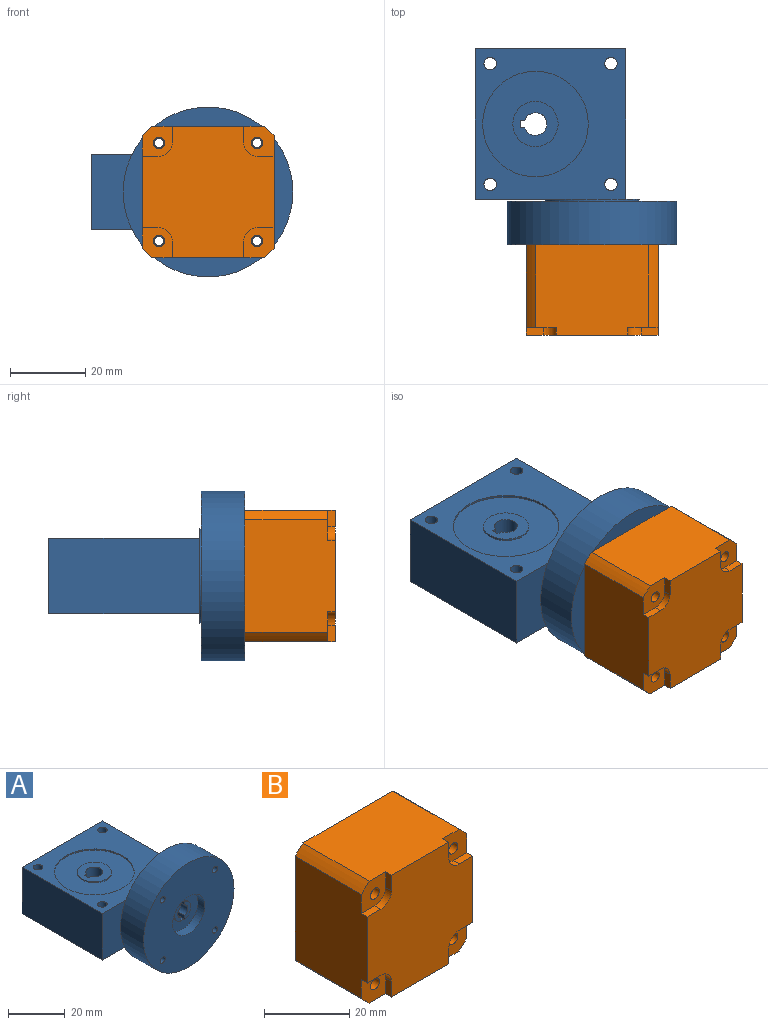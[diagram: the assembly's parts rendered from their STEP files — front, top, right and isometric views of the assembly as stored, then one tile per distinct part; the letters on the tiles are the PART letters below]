
ASSEMBLY  parts=2 mates=1
PART A: 51 faces, bbox 53.5x52x45 mm
  f0: plane 12x12mm, normal (0,0,1), area 82.7mm2, adj f44,f45,f46,f47,f48
  f1: plane 40x40mm, normal (0,0,1), area 950mm2, adj f6,f7,f8,f9,f10,f12,f13,f14
  f2: plane 12x12mm, normal (0,0,-1), area 82.7mm2, adj f43,f44,f45,f46,f47
  f3: cylinder r=4mm len=7.75mm, axis (0,1,0), area 4.2mm2, adj f5,f29,f34,f39
  f4: plane 7.75x3mm, normal (0,-1,0), area 12.3mm2, adj f30,f31,f33,f37
  f5: plane 7.75x3mm, normal (0,-1,0), area 12.3mm2, adj f3,f31,f34,f39
  f6: plane 1.5x1.33mm, normal (0,-1,0), area 0.9mm2, adj f1,f8,f19
  f7: plane 23.5x20mm, normal (0,-1,0), area 400.1mm2, adj f1,f10,f16,f19
  f8: plane 40x20mm, normal (1,0,0), area 800mm2, adj f1,f6,f9,f11,f16,f20
  f9: plane 40x20mm, normal (0,1,0), area 800mm2, adj f1,f8,f10,f16
  f10: plane 40x20mm, normal (-1,0,0), area 800mm2, adj f1,f7,f9,f16
  f11: plane 1.5x1.33mm, normal (0,-1,0), area 0.9mm2, adj f8,f16,f19
  f12: cylinder r=1.65mm len=20mm, axis (0,0,-1), area 207.3mm2, adj f1,f16
  f13: cylinder r=1.65mm len=20mm, axis (0,0,-1), area 207.3mm2, adj f1,f16
  f14: cylinder r=1.65mm len=20mm, axis (0,0,-1), area 207.3mm2, adj f1,f16
  f15: cylinder r=1.65mm len=20mm, axis (0,0,-1), area 207.3mm2, adj f1,f16
  f16: plane 40x40mm, normal (0,0,-1), area 950mm2, adj f7,f8,f9,f10,f11,f12,f13,f14
  f17: plane 15x2.5mm, normal (0,1,0), area 25.5mm2, adj f16,f19
  f18: plane 15x2.5mm, normal (0,1,0), area 25.5mm2, adj f1,f19
  f19: cylinder r=12.5mm len=25mm, axis (0,1,0), area 39.3mm2, adj f6,f7,f11,f17,f18,f20,f23
  f20: plane 17.35x3.5mm, normal (0,1,0), area 41.8mm2, adj f8,f19
  f21: cylinder r=22.5mm len=45mm, axis (0,1,0), area 1625.8mm2, adj f22,f23
  f22: plane 45x45mm, normal (0,-1,0), area 1369.7mm2, adj f21,f24,f25,f26,f27,f28
  f23: plane 45x45mm, normal (0,1,0), area 1079.9mm2, adj f19,f21,f24,f25,f26,f27
  f24: cylinder r=1.25mm len=11.5mm, axis (0,-1,0), area 90.3mm2, adj f22,f23
  f25: cylinder r=1.25mm len=11.5mm, axis (0,-1,0), area 90.3mm2, adj f22,f23
  f26: cylinder r=1.25mm len=11.5mm, axis (0,-1,0), area 90.3mm2, adj f22,f23
  f27: cylinder r=1.25mm len=11.5mm, axis (0,-1,0), area 90.3mm2, adj f22,f23
  f28: cylinder r=8mm len=16mm, axis (0,-1,0), area 170.9mm2, adj f22,f29
  f29: plane 16x16mm, normal (0,-1,0), area 150.8mm2, adj f3,f28,f30,f35,f38
  f30: cylinder r=4mm len=7.75mm, axis (0,1,0), area 4.2mm2, adj f4,f29,f33,f37
  f31: cylinder r=2.5mm len=15mm, axis (0,-1,0), area 215mm2, adj f4,f5,f32,f33,f34,f36,f37,f39
  f32: plane 5x5mm, normal (0,-1,0), area 19.6mm2, adj f31
  f33: plane 5x1.58mm, normal (-1,0,0), area 7.9mm2, adj f4,f30,f31,f35,f36
  f34: plane 5x1.58mm, normal (1,0,0), area 7.9mm2, adj f3,f5,f31,f35,f36
  f35: cylinder r=4mm len=4.6mm, axis (0,-1,0), area 9.3mm2, adj f29,f33,f34,f36
  f36: plane 2x1.71mm, normal (0,-1,0), area 3.1mm2, adj f31,f33,f34,f35
  f37: plane 5x1.58mm, normal (-1,0,0), area 7.9mm2, adj f4,f30,f31,f38,f40
  f38: cylinder r=4mm len=4.6mm, axis (0,-1,0), area 9.3mm2, adj f29,f37,f39,f40
  f39: plane 5x1.58mm, normal (1,0,0), area 7.9mm2, adj f3,f5,f31,f38,f40
  f40: plane 2x1.71mm, normal (0,-1,0), area 3.1mm2, adj f31,f37,f38,f39
  f41: cylinder r=14mm len=28mm, axis (0,0,-1), area 44mm2, adj f16,f42
  f42: plane 28x28mm, normal (0,0,-1), area 502.7mm2, adj f41,f43
  f43: cylinder r=6mm len=12mm, axis (0,0,1), area 18.8mm2, adj f2,f42
  f44: plane 20x1.17mm, normal (0,1,0), area 23.4mm2, adj f0,f2,f45,f47
  f45: plane 20x2mm, normal (1,0,0), area 40mm2, adj f0,f2,f44,f46
  f46: plane 20x1.17mm, normal (0,-1,0), area 23.4mm2, adj f0,f2,f45,f47
  f47: cylinder r=3mm len=20mm, axis (0,0,-1), area 336.2mm2, adj f0,f2,f44,f46
  f48: cylinder r=6mm len=12mm, axis (0,0,1), area 18.8mm2, adj f0,f50
  f49: cylinder r=14mm len=28mm, axis (0,0,1), area 44mm2, adj f1,f50
  f50: plane 28x28mm, normal (0,0,1), area 502.7mm2, adj f48,f49
PART B: 35 faces, bbox 35x39x35 mm
  f0: cylinder r=23mm len=22mm, axis (0,1,0), area 80.2mm2, adj f1,f11,f13,f24
  f1: plane 29.85x24mm, normal (0,0,-1), area 694.7mm2, adj f0,f2,f12,f13,f22,f24,f26,f27
  f2: cylinder r=23mm len=22mm, axis (0,1,0), area 80.2mm2, adj f1,f3,f13,f27
  f3: plane 29.85x24mm, normal (1,0,0), area 694.7mm2, adj f2,f4,f12,f13,f15,f17,f27,f28
  f4: cylinder r=23mm len=22mm, axis (0,1,0), area 80.2mm2, adj f3,f5,f13,f17
  f5: plane 29.85x24mm, normal (0,0,1), area 694.7mm2, adj f4,f6,f12,f13,f16,f17,f20,f21
  f6: cylinder r=23mm len=22mm, axis (0,1,0), area 80.2mm2, adj f5,f11,f13,f21
  f7: cylinder r=1.5mm len=22mm, axis (0,1,0), area 207.3mm2, adj f13,f17
  f8: cylinder r=1.5mm len=22mm, axis (0,1,0), area 207.3mm2, adj f13,f21
  f9: cylinder r=1.5mm len=22mm, axis (0,1,0), area 207.3mm2, adj f13,f24
  f10: cylinder r=1.5mm len=22mm, axis (0,1,0), area 207.3mm2, adj f13,f27
  f11: plane 29.85x24mm, normal (-1,0,0), area 694.7mm2, adj f0,f6,f12,f13,f18,f21,f23,f24
  f12: plane 35x35mm, normal (0,-1,0), area 979.5mm2, adj f1,f3,f5,f11,f14,f15,f16,f18
  f13: plane 35x35mm, normal (0,1,0), area 1105.6mm2, adj f0,f1,f2,f3,f4,f5,f6,f7
  f14: cylinder r=3.5mm len=3.5mm, axis (0,-1,0), area 11mm2, adj f12,f15,f16,f17
  f15: plane 4.5x2mm, normal (0,0,1), area 9mm2, adj f3,f12,f14,f17
  f16: plane 4.5x2mm, normal (1,0,0), area 9mm2, adj f5,f12,f14,f17
  f17: plane 8x8mm, normal (0,-1,0), area 51.2mm2, adj f3,f4,f5,f7,f14,f15,f16
  f18: plane 4.5x2mm, normal (0,0,1), area 9mm2, adj f11,f12,f19,f21
  f19: cylinder r=3.5mm len=3.5mm, axis (0,-1,0), area 11mm2, adj f12,f18,f20,f21
  f20: plane 4.5x2mm, normal (-1,0,0), area 9mm2, adj f5,f12,f19,f21
  f21: plane 8x8mm, normal (0,-1,0), area 51.2mm2, adj f5,f6,f8,f11,f18,f19,f20
  f22: plane 4.5x2mm, normal (-1,0,0), area 9mm2, adj f1,f12,f24,f25
  f23: plane 4.5x2mm, normal (0,0,-1), area 9mm2, adj f11,f12,f24,f25
  f24: plane 8x8mm, normal (0,-1,0), area 51.2mm2, adj f0,f1,f9,f11,f22,f23,f25
  f25: cylinder r=3.5mm len=3.5mm, axis (0,-1,0), area 11mm2, adj f12,f22,f23,f24
  f26: plane 4.5x2mm, normal (1,0,0), area 9mm2, adj f1,f12,f27,f29
  f27: plane 8x8mm, normal (0,-1,0), area 51.2mm2, adj f1,f2,f3,f10,f26,f28,f29
  f28: plane 4.5x2mm, normal (0,0,-1), area 9mm2, adj f3,f12,f27,f29
  f29: cylinder r=3.5mm len=3.5mm, axis (0,-1,0), area 11mm2, adj f12,f26,f27,f28
  f30: cylinder r=5mm len=10mm, axis (0,-1,0), area 62.8mm2, adj f13,f31
  f31: plane 10x10mm, normal (0,1,0), area 71.5mm2, adj f30,f32
  f32: cylinder r=1.5mm len=12.5mm, axis (0,-1,0), area 117.8mm2, adj f31,f34
  f33: plane 2x2mm, normal (0,1,0), area 3.1mm2, adj f34
  f34: cone r=1mm half-angle=45deg, axis (0,-1,0), area 5.6mm2, adj f32,f33
PLACE A t=(17.63,-33.85,23.41)mm fixed
PLACE B t=(34.83,-45.85,-32.09)mm
MATE fastened A.f24 <-> B.f8  axis (0,-1,0) through (-81.71,-45.85,46.41)mm
